# Revit family: Electronics_Desono_Biamp_Column-Line-Source-Loudspeaker_ENT-FR
name_source: partatom
category: Communication Devices
units: mm (PartAtom-declared; Revit-internal decimal feet)

## family parameters
Cut with Voids When Loaded = No
Host = Face
Maintain Annotation Orientation = No
OmniClass Number = 23.85.10.11.14.14.14
OmniClass Title = Loudspeakers
Part Type = Normal
Room Calculation Point = No
Round Connector Dimension = Use Diameter
Shared = No

## types (2) — shared parameters
Baffle Form = Confgurable; straight, curved, and asymmetric curve
Connector Description = NL4MP-type jack; 85V 600W 12Ω (2400W peak)
Continuous Power Handling Nominal Impedance = 85V, 600W @ 12Ω (2400W Peak)
Default Elevation = 4' - 0"
Depth = 0' - 7 1/2"
Description = Desono™ ENT-FR Three-Way, Full-Range Column Line Source Loudspeaker
Environmental = IP54 per IEC 60529, designed in accordance with MIL-STD-810G. Included; ABS plastic rain cover with integrated cable inlet and 1 (25.4 mm) knockout for conduit ingress
Height = 3' - 8 1/2"
Included Accessories = (1) T-Bar mounting bracket (1) Input wiring cover (1) Top connector cover
Input Connection = Top: (1) Dual Banana (male); Bottom: (1) NL4 locking connector; (2) Terminal strip (1) Banana (female)
Manufacturer = Biamp
Nominal Beamwidth  (H x V) = Horizontal: 120°; Vertical: 12° or 6° (user confgurable)
Nominal Maximum SPL (Single unit) = Curved (12°): 120 dB; Straight (6°): 122 dB
Nominal Sensitivity = Curved (12°): 93 dB; Straight (6°): 95 dB
Operating Environment = Indoor or outdoor direct exposure
Operating Mode = Passive
Operating Range = 200 Hz - 20 kHz
Product Documentation Link = https://downloads.biamp.com
Product Page URL = https://www.biamp.com
Product data url = https://www.bimobject.com
Recommended Amplifers = 600W - 1200W @ 12Ω (85V - 120V)
Required Accessories = Digital Signal Processor / External High Pass Filter - 200Hz, 12 dB /octave
Transducers = LF: Six 3.5 neodymium; MF: Eighteen 2.35; HF: Forty-two 1 (six 7 long by 1 wide planar-coupled Compact Ribbon Emulators)
Typical SPL at 100 feet (30 meters) = 96 dB
URL = https://www.biamp.com
Weight = 40.00 lb
Width = 0' - 5 1/2"

## per-type parameters (varying)
| type | Bracket Material | Grill Material | Housing Material |
| ENT-FR B | Biamp - Metal - Black | Biamp - Plastic - Black(Grid) | Biamp - Plastic - Black |
| ENT-FR W | Biamp - Metal - White | Biamp - Plastic - White(Grid) | Biamp - Plastic - White |

note: column(s) folded — value = type name in every type: Model

## geometry (parser evidence)
native form markers: Sweep x2
no freeform markers — native parametric forms only
